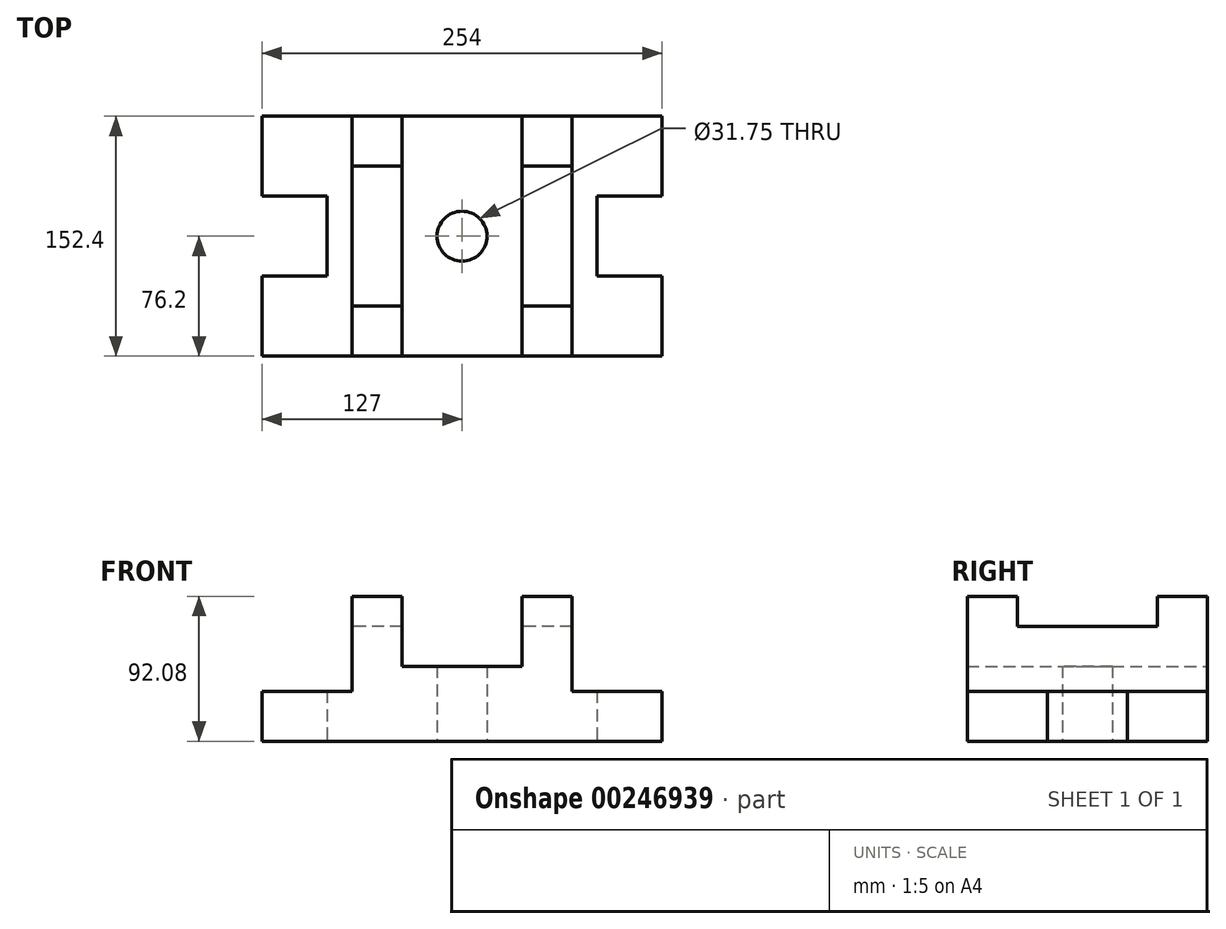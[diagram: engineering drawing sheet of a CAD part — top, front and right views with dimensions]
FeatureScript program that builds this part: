
annotation { "Feature Type Name" : "Feature", "Feature Type Description" : "" }
export const myFeature = defineFeature(function(context is Context, id is Id, definition is map)
    precondition{}
    {
        {
            var Q0;
            Q0=qCreatedBy(makeId("Top.planeOp"),FACE);
            var sketch = newSketch(context, id + "F0", { "sketchPlane" : qUnion([Q0])});
            skLineSegment(sketch, "E0", {"start": v(-127, 76.2) * mm, "end": v(127, 76.2) * mm});
            skLineSegment(sketch, "E1", {"start": v(127, 76.2) * mm, "end": v(127, 25.4) * mm});
            skLineSegment(sketch, "E2", {"start": v(85.73, 25.4) * mm, "end": v(127, 25.4) * mm});
            skLineSegment(sketch, "E3", {"start": v(85.73, 25.4) * mm, "end": v(85.72, -25.4) * mm});
            skLineSegment(sketch, "E4", {"start": v(85.72, -25.4) * mm, "end": v(127, -25.4) * mm});
            skLineSegment(sketch, "E5", {"start": v(127, -76.2) * mm, "end": v(127, -25.4) * mm});
            skLineSegment(sketch, "E6", {"start": v(127, -76.2) * mm, "end": v(-127, -76.2) * mm});
            skLineSegment(sketch, "E7", {"start": v(-127, -76.2) * mm, "end": v(-127, -25.4) * mm});
            skLineSegment(sketch, "E8", {"start": v(-127, -25.4) * mm, "end": v(-85.72, -25.4) * mm});
            skLineSegment(sketch, "E9", {"start": v(-85.72, -25.4) * mm, "end": v(-85.72, 25.4) * mm});
            skLineSegment(sketch, "E10", {"start": v(-85.72, 25.4) * mm, "end": v(-127, 25.4) * mm});
            skLineSegment(sketch, "E11", {"start": v(-127, 25.4) * mm, "end": v(-127, 76.2) * mm});
            skCircle(sketch, "E12", {"center": v(0, 0) * mm, "radius": 15.88 * mm});
            skPoint(sketch, "E13.endSnap0", {"position": v(0, -76.2) * mm});
            skLineSegment(sketch, "E14", {"start": v(0, 0) * mm, "end": v(0, -76.2) * mm, "construction": true});
            skLineSegment(sketch, "E15", {"start": v(69.85, 76.2) * mm, "end": v(69.85, -76.2) * mm});
            skLineSegment(sketch, "E16", {"start": v(38.1, 76.2) * mm, "end": v(38.1, -76.2) * mm});
            skLineSegment(sketch, "E17", {"start": v(-38.1, 76.2) * mm, "end": v(-38.1, -76.2) * mm});
            skLineSegment(sketch, "E18", {"start": v(-69.85, 76.2) * mm, "end": v(-69.85, -76.2) * mm});
            skLineSegment(sketch, "E19", {"start": v(-69.85, 44.45) * mm, "end": v(-38.1, 44.45) * mm});
            skLineSegment(sketch, "E20", {"start": v(-69.85, -44.45) * mm, "end": v(-38.1, -44.45) * mm});
            skLineSegment(sketch, "E21", {"start": v(38.1, 44.45) * mm, "end": v(69.85, 44.45) * mm});
            skLineSegment(sketch, "E22", {"start": v(38.1, -44.45) * mm, "end": v(69.85, -44.45) * mm});
            skSolve(sketch);
        }
        {
            var Q0;
            Q0=makeQuery(id+"F0.imprint","IMPRINT",FACE,{"disambiguationData":[TD([[makeQuery(id+"F0.imprint","IMPRINT",EDGE,{"derivedFrom":sQuery(id+"F0.wireOp",EDGE,"E0")}),-1.0]])]});
            var Q1;
            {var subQ0=sQuery(id+"F0.wireOp",EDGE,"E7");Q1=makeQuery(id+"F0.imprint","IMPRINT",FACE,{"disambiguationData":[TD([[makeQuery(id+"F0.imprint","IMPRINT",EDGE,{"derivedFrom":subQ0}),-1.0]])]});}
            var Q2;
            {var subQ0=sQuery(id+"F0.wireOp",EDGE,"E19");Q2=makeQuery(id+"F0.imprint","IMPRINT",FACE,{"disambiguationData":[TD([[makeQuery(id+"F0.imprint","IMPRINT",EDGE,{"derivedFrom":subQ0}),-1.0]])]});}
            var Q3;
            {var subQ5=sQuery(id+"F0.wireOp",EDGE,"E20");Q3=makeQuery(id+"F0.imprint","IMPRINT",FACE,{"disambiguationData":[TD([[makeQuery(id+"F0.imprint","IMPRINT",EDGE,{"derivedFrom":subQ5}),-1.0]])]});}
            var Q4;
            Q4=makeQuery(id+"F0.imprint","IMPRINT",FACE,{"disambiguationData":[TD([[makeQuery(id+"F0.imprint","IMPRINT",EDGE,{"derivedFrom":sQuery(id+"F0.wireOp",EDGE,"E12")}),-1.0]])]});
            var Q5;
            {var subQ0=sQuery(id+"F0.wireOp",EDGE,"E21");Q5=makeQuery(id+"F0.imprint","IMPRINT",FACE,{"disambiguationData":[TD([[makeQuery(id+"F0.imprint","IMPRINT",EDGE,{"derivedFrom":subQ0}),-1.0]])]});}
            var Q6;
            {var subQ5=sQuery(id+"F0.wireOp",EDGE,"E22");Q6=makeQuery(id+"F0.imprint","IMPRINT",FACE,{"disambiguationData":[TD([[makeQuery(id+"F0.imprint","IMPRINT",EDGE,{"derivedFrom":subQ5}),-1.0]])]});}
            var Q7;
            {var subQ0=sQuery(id+"F0.wireOp",EDGE,"E1");Q7=makeQuery(id+"F0.imprint","IMPRINT",FACE,{"disambiguationData":[TD([[makeQuery(id+"F0.imprint","IMPRINT",EDGE,{"derivedFrom":subQ0}),-1.0]])]});}
            extrude(context, id + "F1", {"entities" : qUnion([Q0, Q1, Q2, Q3, Q4, Q5, Q6, Q7]), "depth" : 31.75 * mm});
        }
        {
            var Q0;
            {var subQ5=sQuery(id+"F0.wireOp",EDGE,"E19");Q0=makeQuery(id+"F0.imprint","IMPRINT",FACE,{"disambiguationData":[TD([[makeQuery(id+"F0.imprint","IMPRINT",EDGE,{"derivedFrom":subQ5}),1.0]])]});}
            var Q1;
            {var subQ0=sQuery(id+"F0.wireOp",EDGE,"E19");Q1=makeQuery(id+"F0.imprint","IMPRINT",FACE,{"disambiguationData":[TD([[makeQuery(id+"F0.imprint","IMPRINT",EDGE,{"derivedFrom":subQ0}),-1.0]])]});}
            var Q2;
            {var subQ5=sQuery(id+"F0.wireOp",EDGE,"E20");Q2=makeQuery(id+"F0.imprint","IMPRINT",FACE,{"disambiguationData":[TD([[makeQuery(id+"F0.imprint","IMPRINT",EDGE,{"derivedFrom":subQ5}),-1.0]])]});}
            var Q3;
            Q3=makeQuery(id+"F0.imprint","IMPRINT",FACE,{"disambiguationData":[TD([[makeQuery(id+"F0.imprint","IMPRINT",EDGE,{"derivedFrom":sQuery(id+"F0.wireOp",EDGE,"E12")}),-1.0]])]});
            var Q4;
            {var subQ5=sQuery(id+"F0.wireOp",EDGE,"E22");Q4=makeQuery(id+"F0.imprint","IMPRINT",FACE,{"disambiguationData":[TD([[makeQuery(id+"F0.imprint","IMPRINT",EDGE,{"derivedFrom":subQ5}),-1.0]])]});}
            var Q5;
            {var subQ0=sQuery(id+"F0.wireOp",EDGE,"E21");Q5=makeQuery(id+"F0.imprint","IMPRINT",FACE,{"disambiguationData":[TD([[makeQuery(id+"F0.imprint","IMPRINT",EDGE,{"derivedFrom":subQ0}),-1.0]])]});}
            var Q6;
            {var subQ5=sQuery(id+"F0.wireOp",EDGE,"E21");Q6=makeQuery(id+"F0.imprint","IMPRINT",FACE,{"disambiguationData":[TD([[makeQuery(id+"F0.imprint","IMPRINT",EDGE,{"derivedFrom":subQ5}),1.0]])]});}
            extrude(context, id + "F2", {"entities" : qUnion([Q0, Q1, Q2, Q3, Q4, Q5, Q6]), "operationType" : NewBodyOperationType.ADD, "depth" : 47.62 * mm});
        }
        {
            var Q0;
            {var subQ5=sQuery(id+"F0.wireOp",EDGE,"E19");Q0=makeQuery(id+"F0.imprint","IMPRINT",FACE,{"disambiguationData":[TD([[makeQuery(id+"F0.imprint","IMPRINT",EDGE,{"derivedFrom":subQ5}),1.0]])]});}
            var Q1;
            {var subQ0=sQuery(id+"F0.wireOp",EDGE,"E19");Q1=makeQuery(id+"F0.imprint","IMPRINT",FACE,{"disambiguationData":[TD([[makeQuery(id+"F0.imprint","IMPRINT",EDGE,{"derivedFrom":subQ0}),-1.0]])]});}
            var Q2;
            {var subQ5=sQuery(id+"F0.wireOp",EDGE,"E20");Q2=makeQuery(id+"F0.imprint","IMPRINT",FACE,{"disambiguationData":[TD([[makeQuery(id+"F0.imprint","IMPRINT",EDGE,{"derivedFrom":subQ5}),-1.0]])]});}
            var Q3;
            {var subQ5=sQuery(id+"F0.wireOp",EDGE,"E21");Q3=makeQuery(id+"F0.imprint","IMPRINT",FACE,{"disambiguationData":[TD([[makeQuery(id+"F0.imprint","IMPRINT",EDGE,{"derivedFrom":subQ5}),1.0]])]});}
            var Q4;
            {var subQ0=sQuery(id+"F0.wireOp",EDGE,"E21");Q4=makeQuery(id+"F0.imprint","IMPRINT",FACE,{"disambiguationData":[TD([[makeQuery(id+"F0.imprint","IMPRINT",EDGE,{"derivedFrom":subQ0}),-1.0]])]});}
            var Q5;
            {var subQ5=sQuery(id+"F0.wireOp",EDGE,"E22");Q5=makeQuery(id+"F0.imprint","IMPRINT",FACE,{"disambiguationData":[TD([[makeQuery(id+"F0.imprint","IMPRINT",EDGE,{"derivedFrom":subQ5}),-1.0]])]});}
            extrude(context, id + "F3", {"entities" : qUnion([Q0, Q1, Q2, Q3, Q4, Q5]), "operationType" : NewBodyOperationType.ADD, "depth" : 73.02 * mm});
        }
        {
            var Q0;
            {var subQ5=sQuery(id+"F0.wireOp",EDGE,"E19");Q0=makeQuery(id+"F0.imprint","IMPRINT",FACE,{"disambiguationData":[TD([[makeQuery(id+"F0.imprint","IMPRINT",EDGE,{"derivedFrom":subQ5}),1.0]])]});}
            var Q1;
            {var subQ5=sQuery(id+"F0.wireOp",EDGE,"E20");Q1=makeQuery(id+"F0.imprint","IMPRINT",FACE,{"disambiguationData":[TD([[makeQuery(id+"F0.imprint","IMPRINT",EDGE,{"derivedFrom":subQ5}),-1.0]])]});}
            var Q2;
            {var subQ5=sQuery(id+"F0.wireOp",EDGE,"E21");Q2=makeQuery(id+"F0.imprint","IMPRINT",FACE,{"disambiguationData":[TD([[makeQuery(id+"F0.imprint","IMPRINT",EDGE,{"derivedFrom":subQ5}),1.0]])]});}
            var Q3;
            {var subQ5=sQuery(id+"F0.wireOp",EDGE,"E22");Q3=makeQuery(id+"F0.imprint","IMPRINT",FACE,{"disambiguationData":[TD([[makeQuery(id+"F0.imprint","IMPRINT",EDGE,{"derivedFrom":subQ5}),-1.0]])]});}
            extrude(context, id + "F4", {"entities" : qUnion([Q0, Q1, Q2, Q3]), "operationType" : NewBodyOperationType.ADD, "depth" : 92.07 * mm});
        }
    });
